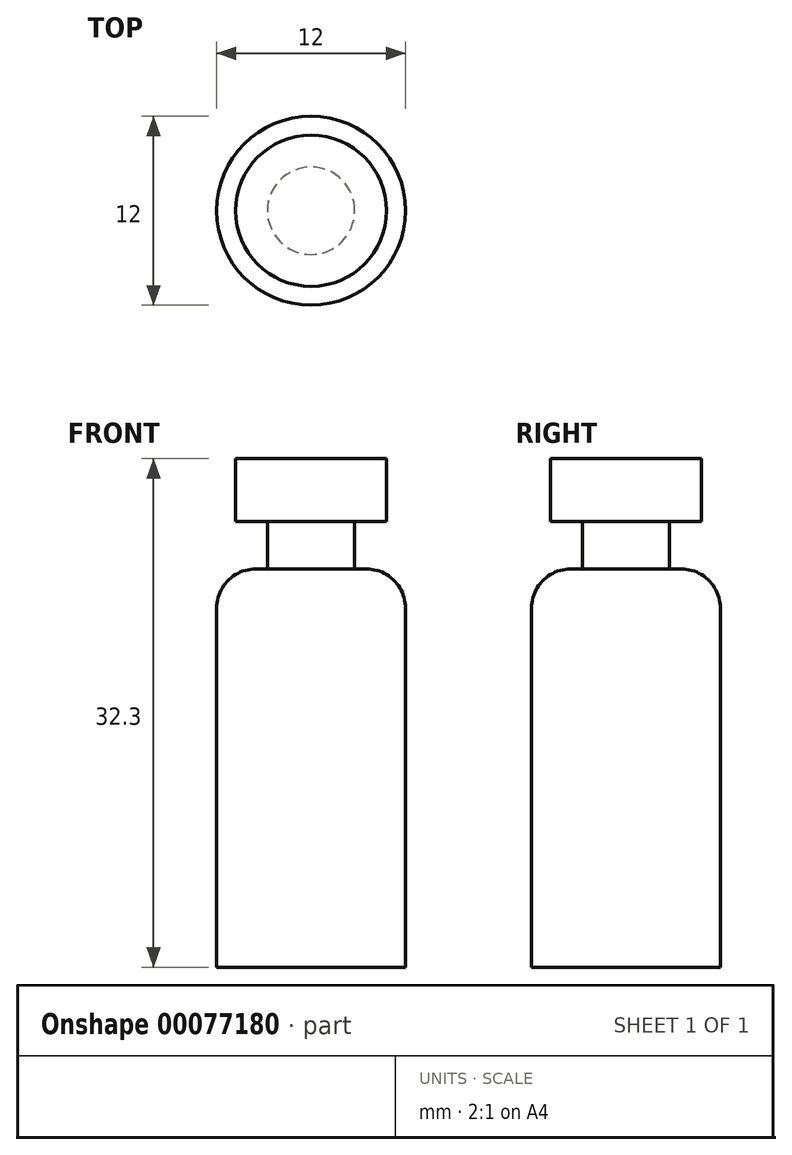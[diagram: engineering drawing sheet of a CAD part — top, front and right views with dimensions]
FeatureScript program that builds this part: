
annotation { "Feature Type Name" : "Feature", "Feature Type Description" : "" }
export const myFeature = defineFeature(function(context is Context, id is Id, definition is map)
    precondition{}
    {
        {
            var Q0;
            Q0=qCreatedBy(makeId("Front.planeOp"),FACE);
            var sketch = newSketch(context, id + "F0", { "sketchPlane" : qUnion([Q0])});
            skLineSegment(sketch, "E0", {"start": v(0, 0) * mm, "end": v(6, 0) * mm});
            skLineSegment(sketch, "E1", {"start": v(6, 0) * mm, "end": v(6, 25.3) * mm});
            skLineSegment(sketch, "E2", {"start": v(6, 25.3) * mm, "end": v(2.77, 25.3) * mm});
            skLineSegment(sketch, "E3", {"start": v(2.77, 25.3) * mm, "end": v(2.77, 28.3) * mm});
            skLineSegment(sketch, "E4", {"start": v(2.77, 28.3) * mm, "end": v(4.8, 28.3) * mm});
            skLineSegment(sketch, "E5", {"start": v(4.8, 28.3) * mm, "end": v(4.8, 32.3) * mm});
            skLineSegment(sketch, "E6", {"start": v(4.8, 32.3) * mm, "end": v(0, 32.3) * mm});
            skLineSegment(sketch, "E7", {"start": v(0, 32.3) * mm, "end": v(0, 0) * mm});
            skLineSegment(sketch, "E8", {"start": v(0, 0) * mm, "end": v(0, 41.13) * mm, "construction": true});
            skSolve(sketch);
        }
        {
            var Q0;
            Q0=qSketchRegion(id+"F0",true);
            var Q1;
            Q1=sQuery(id+"F0.wireOp",EDGE,"E8");
            revolve(context, id + "F1", {"entities" : qUnion([Q0]), "axis" : qUnion([Q1]), "revolveType" : RevolveType.FULL});
        }
        {
            var Q0;
            Q0=makeQuery(id+"F1.opRevolve","SWEPT_EDGE",EDGE,{"disambiguationData":[OSD([sQuery(id+"F0.wireOp",EDGE,"E1"),sQuery(id+"F0.wireOp",EDGE,"E2")])]});
            fillet(context, id + "F2", {"entities" : qUnion([Q0]), "radius" : 2.5 * mm, "tangentPropagation" : true, "allowEdgeOverflow" : false});
        }
    });
